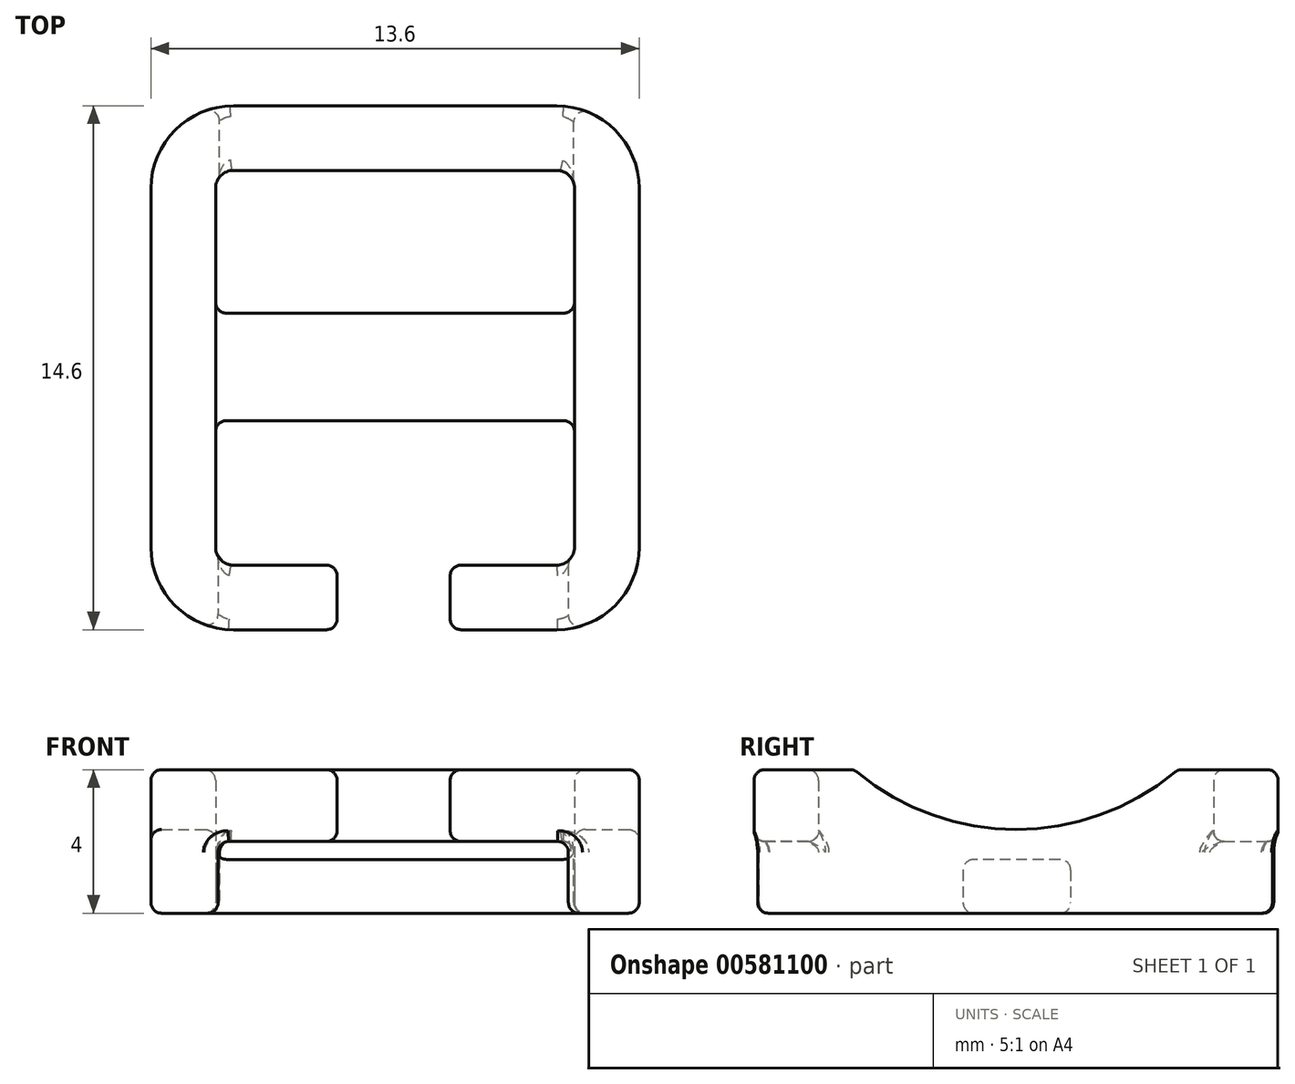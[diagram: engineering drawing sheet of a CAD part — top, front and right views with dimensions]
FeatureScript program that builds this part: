
annotation { "Feature Type Name" : "Feature", "Feature Type Description" : "" }
export const myFeature = defineFeature(function(context is Context, id is Id, definition is map)
    precondition{}
    {
        {
            var Q0;
            Q0=qCreatedBy(makeId("Top.planeOp"),FACE);
            var sketch = newSketch(context, id + "F0", { "sketchPlane" : qUnion([Q0])});
            skPoint(sketch, "E0.middle", {"position": v(0, 0) * mm});
            skLineSegment(sketch, "E1.bottom", {"start": v(-4.5, 5.5) * mm, "end": v(4.5, 5.5) * mm});
            skLineSegment(sketch, "E1.top", {"start": v(-4.5, -5.5) * mm, "end": v(4.5, -5.5) * mm});
            skLineSegment(sketch, "E1.left", {"start": v(-5, 5) * mm, "end": v(-5, -5) * mm});
            skLineSegment(sketch, "E1.right", {"start": v(5, 5) * mm, "end": v(5, -5) * mm});
            skPoint(sketch, "E2.visualSharp", {"position": v(-5, 5.5) * mm});
            skArc(sketch, "E2.filletArc", {"start": v(-4.5, 5.5) * mm, "mid": v(-4.85, 5.35) * mm, "end": v(-5, 5) * mm});
            skPoint(sketch, "E3.visualSharp", {"position": v(5, 5.5) * mm});
            skArc(sketch, "E3.filletArc", {"start": v(5, 5) * mm, "mid": v(4.85, 5.35) * mm, "end": v(4.5, 5.5) * mm});
            skPoint(sketch, "E4.visualSharp", {"position": v(5, -5.5) * mm});
            skArc(sketch, "E4.filletArc", {"start": v(4.5, -5.5) * mm, "mid": v(4.85, -5.35) * mm, "end": v(5, -5) * mm});
            skPoint(sketch, "E5.visualSharp", {"position": v(-5, -5.5) * mm});
            skArc(sketch, "E5.filletArc", {"start": v(-5, -5) * mm, "mid": v(-4.85, -5.35) * mm, "end": v(-4.5, -5.5) * mm});
            skArc(sketch, "E6.0", {"start": v(-4.5, 7.3) * mm, "mid": v(-6.13, 6.63) * mm, "end": v(-6.8, 5) * mm});
            skLineSegment(sketch, "E6.1", {"start": v(-6.8, 5) * mm, "end": v(-6.8, -5) * mm});
            skLineSegment(sketch, "E6.2", {"start": v(-4.5, 7.3) * mm, "end": v(4.5, 7.3) * mm});
            skArc(sketch, "E6.3", {"start": v(-6.8, -5) * mm, "mid": v(-6.13, -6.63) * mm, "end": v(-4.5, -7.3) * mm});
            skArc(sketch, "E6.4", {"start": v(6.8, 5) * mm, "mid": v(6.13, 6.63) * mm, "end": v(4.5, 7.3) * mm});
            skLineSegment(sketch, "E6.5", {"start": v(6.8, 5) * mm, "end": v(6.8, -5) * mm});
            skArc(sketch, "E6.6", {"start": v(4.5, -7.3) * mm, "mid": v(6.13, -6.63) * mm, "end": v(6.8, -5) * mm});
            skLineSegment(sketch, "E6.7", {"start": v(-4.5, -7.3) * mm, "end": v(4.5, -7.3) * mm});
            skSolve(sketch);
        }
        {
            var Q0;
            Q0=makeQuery(id+"F0.imprint","IMPRINT",FACE,{"disambiguationData":[TD([[makeQuery(id+"F0.imprint","IMPRINT",EDGE,{"derivedFrom":sQuery(id+"F0.wireOp",EDGE,"E1.bottom")}),1.0]])]});
            extrude(context, id + "F1", {"entities" : qUnion([Q0]), "endBound" : BoundingType.SYMMETRIC, "depth" : 4 * mm, "offsetDistance" : 25 * mm});
        }
        {
            var Q0;
            Q0=makeQuery(id+"F1.opExtrude","SWEPT_FACE",FACE,{"disambiguationData":[OSD([sQuery(id+"F0.wireOp",EDGE,"E6.5")])]});
            var sketch = newSketch(context, id + "F2", { "sketchPlane" : qUnion([Q0])});
            skCircle(sketch, "E7", {"center": v(0, 7.27) * mm, "radius": 6.94 * mm});
            skSolve(sketch);
        }
        {
            var Q0;
            Q0 = qSketchRegion(id + "F2", true);
            extrude(context, id + "F3", {"entities" : qUnion([Q0]), "operationType" : NewBodyOperationType.REMOVE, "oppositeDirection" : true, "depth" : 17 * mm, "offsetDistance" : 25 * mm});
        }
        {
            var Q0;
            Q0=makeQuery(id+"F1.opExtrude","SWEPT_FACE",FACE,{"disambiguationData":[OSD([sQuery(id+"F0.wireOp",EDGE,"E1.right")])]});
            var sketch = newSketch(context, id + "F4", { "sketchPlane" : qUnion([Q0])});
            skLineSegment(sketch, "E8.bottom", {"start": v(-1.52, -0.5) * mm, "end": v(1.48, -0.5) * mm});
            skLineSegment(sketch, "E8.top", {"start": v(-1.52, -2) * mm, "end": v(1.48, -2) * mm});
            skLineSegment(sketch, "E8.left", {"start": v(-1.52, -0.5) * mm, "end": v(-1.52, -2) * mm});
            skLineSegment(sketch, "E8.right", {"start": v(1.48, -0.5) * mm, "end": v(1.48, -2) * mm});
            skSolve(sketch);
        }
        {
            var Q0;
            Q0=makeQuery(id+"F4.imprint","IMPRINT",FACE,{"disambiguationData":[TD([[makeQuery(id+"F4.imprint","IMPRINT",EDGE,{"derivedFrom":sQuery(id+"F4.wireOp",EDGE,"E8.bottom")}),-1.0]])]});
            var Q1;
            Q1=sQuery(id+"F4.wireOp",EDGE,"E8.bottom");
            var Q2;
            Q2=sQuery(id+"F4.wireOp",EDGE,"E8.right");
            var Q3;
            Q3=sQuery(id+"F4.wireOp",EDGE,"E8.top");
            var Q4;
            Q4=sQuery(id+"F4.wireOp",EDGE,"E8.left");
            extrude(context, id + "F5", {"entities" : qUnion([Q0]), "operationType" : NewBodyOperationType.ADD, "surfaceEntities" : qUnion([Q1, Q2, Q3, Q4]), "depth" : 10.1 * mm, "offsetDistance" : 25 * mm});
        }
        {
            var Q0;
            Q0=makeQuery(id+"F1.opExtrude","SWEPT_FACE",FACE,{"disambiguationData":[OSD([sQuery(id+"F0.wireOp",EDGE,"E6.7")])]});
            var sketch = newSketch(context, id + "F6", { "sketchPlane" : qUnion([Q0])});
            skLineSegment(sketch, "E9.bottom", {"start": v(-4.93, 0) * mm, "end": v(4.83, 0) * mm});
            skLineSegment(sketch, "E9.top", {"start": v(-4.93, -2) * mm, "end": v(4.83, -2) * mm});
            skLineSegment(sketch, "E9.left", {"start": v(-4.93, 0) * mm, "end": v(-4.93, -2) * mm});
            skLineSegment(sketch, "E9.right", {"start": v(4.83, 0) * mm, "end": v(4.83, -2) * mm});
            skSolve(sketch);
        }
        {
            var Q0;
            Q0 = qSketchRegion(id + "F6", true);
            extrude(context, id + "F7", {"entities" : qUnion([Q0]), "operationType" : NewBodyOperationType.REMOVE, "oppositeDirection" : true, "depth" : 2.8 * mm, "offsetDistance" : 25 * mm});
        }
        {
            var Q0;
            Q0=makeQuery(id+"F1.opExtrude","SWEPT_FACE",FACE,{"disambiguationData":[OSD([sQuery(id+"F0.wireOp",EDGE,"E6.2")])]});
            var sketch = newSketch(context, id + "F8", { "sketchPlane" : qUnion([Q0])});
            skLineSegment(sketch, "E10.bottom", {"start": v(-4.98, 0) * mm, "end": v(4.89, 0) * mm});
            skLineSegment(sketch, "E10.top", {"start": v(-4.98, -2) * mm, "end": v(4.89, -2) * mm});
            skLineSegment(sketch, "E10.left", {"start": v(-4.98, 0) * mm, "end": v(-4.98, -2) * mm});
            skLineSegment(sketch, "E10.right", {"start": v(4.89, 0) * mm, "end": v(4.89, -2) * mm});
            skSolve(sketch);
        }
        {
            var Q0;
            Q0 = qSketchRegion(id + "F8", true);
            extrude(context, id + "F9", {"entities" : qUnion([Q0]), "operationType" : NewBodyOperationType.REMOVE, "oppositeDirection" : true, "depth" : 2.4 * mm, "offsetDistance" : 25 * mm});
        }
        {
            var Q0;
            {var subQ0=sQuery(id+"F0.wireOp",EDGE,"E6.7");var subQ1=sQuery(id+"F0.wireOp",EDGE,"E6.3");var subQ2=sQuery(id+"F0.wireOp",EDGE,"E6.1");var subQ3=sQuery(id+"F0.wireOp",EDGE,"E5.filletArc");var subQ4=sQuery(id+"F0.wireOp",EDGE,"E1.top");var subQ5=sQuery(id+"F0.wireOp",EDGE,"E4.filletArc");var subQ6=sQuery(id+"F0.wireOp",EDGE,"E6.5");var subQ7=sQuery(id+"F0.wireOp",EDGE,"E1.left");var subQ8=sQuery(id+"F0.wireOp",EDGE,"E6.6");var subQ9=sQuery(id+"F0.wireOp",EDGE,"E1.right");Q0=makeQuery(id+"F3.boolean.opBoolean","SPLIT",FACE,{"disambiguationData":[TD([makeQuery(id+"F1.opExtrude","SWEPT_FACE",FACE,{"disambiguationData":[OSD([subQ4])]})])],"derivedFrom":makeQuery(id+"F1.opExtrude","CAP_FACE",FACE,{"disambiguationData":[OSD([sQuery(id+"F0.wireOp",EDGE,"E1.bottom"),subQ4,subQ7,subQ9,sQuery(id+"F0.wireOp",EDGE,"E2.filletArc"),sQuery(id+"F0.wireOp",EDGE,"E3.filletArc"),subQ5,subQ3,sQuery(id+"F0.wireOp",EDGE,"E6.0"),subQ2,sQuery(id+"F0.wireOp",EDGE,"E6.2"),subQ1,sQuery(id+"F0.wireOp",EDGE,"E6.4"),subQ6,subQ8,subQ0])],"isStart":false})});}
            var sketch = newSketch(context, id + "F10", { "sketchPlane" : qUnion([Q0])});
            skLineSegment(sketch, "E11.bottom", {"start": v(-1.61, -5.5) * mm, "end": v(1.54, -5.5) * mm});
            skLineSegment(sketch, "E11.top", {"start": v(-1.61, -7.3) * mm, "end": v(1.54, -7.3) * mm});
            skLineSegment(sketch, "E11.left", {"start": v(-1.61, -5.5) * mm, "end": v(-1.61, -7.3) * mm});
            skLineSegment(sketch, "E11.right", {"start": v(1.54, -5.5) * mm, "end": v(1.54, -7.3) * mm});
            skSolve(sketch);
        }
        {
            var Q0;
            Q0 = qSketchRegion(id + "F10", true);
            extrude(context, id + "F11", {"entities" : qUnion([Q0]), "operationType" : NewBodyOperationType.REMOVE, "oppositeDirection" : true, "depth" : 2.3 * mm, "offsetDistance" : 25 * mm});
        }
        {
            var Q0;
            Q0=makeQuery(id+"F5.opExtrude","SWEPT_FACE",FACE,{"disambiguationData":[OSD([sQuery(id+"F4.wireOp",EDGE,"E8.top")])]});
            var Q1;
            Q1=makeQuery(id+"F5.opExtrude","SWEPT_EDGE",EDGE,{"disambiguationData":[OSD([sQuery(id+"F4.wireOp",VERTEX,"E8.right.start")])]});
            var Q2;
            Q2=makeQuery(id+"F5.opExtrude","SWEPT_FACE",FACE,{"disambiguationData":[OSD([sQuery(id+"F4.wireOp",EDGE,"E8.right")])]});
            var Q3;
            Q3=makeQuery(id+"F5.opExtrude","SWEPT_EDGE",EDGE,{"disambiguationData":[OSD([sQuery(id+"F4.wireOp",VERTEX,"E8.top.end")])]});
            var Q4;
            Q4=makeQuery(id+"F5.opExtrude","SWEPT_FACE",FACE,{"disambiguationData":[OSD([sQuery(id+"F4.wireOp",EDGE,"E8.bottom")])]});
            var Q5;
            Q5=makeQuery(id+"F5.opExtrude","SWEPT_EDGE",EDGE,{"disambiguationData":[OSD([sQuery(id+"F4.wireOp",VERTEX,"E8.left.start")])]});
            var Q6;
            Q6=makeQuery(id+"F1.opExtrude","CAP_EDGE",EDGE,{"disambiguationData":[OSD([sQuery(id+"F0.wireOp",EDGE,"E6.2")])],"isStart":false});
            var Q7;
            Q7=makeQuery(id+"F3.boolean.opBoolean","INTERSECT",EDGE,{"derivedFrom":[makeQuery(id+"F1.opExtrude","SWEPT_FACE",FACE,{"disambiguationData":[OSD([sQuery(id+"F0.wireOp",EDGE,"E1.left")])]}),makeQuery(id+"F3.opExtrude","SWEPT_FACE",FACE,{"disambiguationData":[OSD([sQuery(id+"F2.wireOp",EDGE,"E7")])]})]});
            var Q8;
            Q8=makeQuery(id+"F1.opExtrude","SWEPT_FACE",FACE,{"disambiguationData":[OSD([sQuery(id+"F0.wireOp",EDGE,"E1.left")])]});
            var Q9;
            Q9=makeQuery(id+"F1.opExtrude","CAP_EDGE",EDGE,{"disambiguationData":[OSD([sQuery(id+"F0.wireOp",EDGE,"E1.left")])],"isStart":true});
            var Q10;
            Q10=makeQuery(id+"F1.opExtrude","CAP_EDGE",EDGE,{"disambiguationData":[OSD([sQuery(id+"F0.wireOp",EDGE,"E1.bottom")])],"isStart":false});
            var Q11;
            Q11=makeQuery(id+"F1.opExtrude","SWEPT_FACE",FACE,{"disambiguationData":[OSD([sQuery(id+"F0.wireOp",EDGE,"E1.bottom")])]});
            var Q12;
            Q12=makeQuery(id+"F3.boolean.opBoolean","COPY",EDGE,{"derivedFrom":makeQuery(id+"F3.opExtrude","CAP_EDGE",EDGE,{"disambiguationData":[OSD([sQuery(id+"F2.wireOp",EDGE,"E7")])],"isStart":true})});
            var Q13;
            Q13=makeQuery(id+"F1.opExtrude","CAP_EDGE",EDGE,{"disambiguationData":[OSD([sQuery(id+"F0.wireOp",EDGE,"E6.5")])],"isStart":true});
            var Q14;
            Q14=makeQuery(id+"F7.boolean.opBoolean","COPY",FACE,{"derivedFrom":makeQuery(id+"F7.opExtrude","SWEPT_FACE",FACE,{"disambiguationData":[OSD([sQuery(id+"F6.wireOp",EDGE,"E9.right")])]})});
            var Q15;
            Q15=makeQuery(id+"F9.boolean.opBoolean","COPY",FACE,{"derivedFrom":makeQuery(id+"F9.opExtrude","SWEPT_FACE",FACE,{"disambiguationData":[OSD([sQuery(id+"F8.wireOp",EDGE,"E10.right")])]})});
            var Q16;
            {var subQ0=sQuery(id+"F6.wireOp",EDGE,"E9.bottom");Q16=makeQuery(id+"F11.boolean.opBoolean","SPLIT",EDGE,{"disambiguationData":[TD([makeQuery(id+"F1.opExtrude","SWEPT_FACE",FACE,{"disambiguationData":[OSD([sQuery(id+"F0.wireOp",EDGE,"E6.6")])]})])],"derivedFrom":makeQuery(id+"F7.boolean.opBoolean","COPY",EDGE,{"derivedFrom":makeQuery(id+"F7.opExtrude","CAP_EDGE",EDGE,{"disambiguationData":[OSD([subQ0])],"isStart":true})})});}
            var Q17;
            Q17=makeQuery(id+"F3.boolean.opBoolean","INTERSECT",EDGE,{"disambiguationData":[OD(2.0)],"derivedFrom":[makeQuery(id+"F1.opExtrude","CAP_FACE",FACE,{"disambiguationData":[OSD([sQuery(id+"F0.wireOp",EDGE,"E1.bottom"),sQuery(id+"F0.wireOp",EDGE,"E1.top"),sQuery(id+"F0.wireOp",EDGE,"E1.left"),sQuery(id+"F0.wireOp",EDGE,"E1.right"),sQuery(id+"F0.wireOp",EDGE,"E2.filletArc"),sQuery(id+"F0.wireOp",EDGE,"E3.filletArc"),sQuery(id+"F0.wireOp",EDGE,"E4.filletArc"),sQuery(id+"F0.wireOp",EDGE,"E5.filletArc"),sQuery(id+"F0.wireOp",EDGE,"E6.0"),sQuery(id+"F0.wireOp",EDGE,"E6.1"),sQuery(id+"F0.wireOp",EDGE,"E6.2"),sQuery(id+"F0.wireOp",EDGE,"E6.3"),sQuery(id+"F0.wireOp",EDGE,"E6.4"),sQuery(id+"F0.wireOp",EDGE,"E6.5"),sQuery(id+"F0.wireOp",EDGE,"E6.6"),sQuery(id+"F0.wireOp",EDGE,"E6.7")])],"isStart":false}),makeQuery(id+"F3.opExtrude","SWEPT_FACE",FACE,{"disambiguationData":[OSD([sQuery(id+"F2.wireOp",EDGE,"E7")])]})]});
            var Q18;
            Q18=makeQuery(id+"F11.boolean.opBoolean","COPY",FACE,{"derivedFrom":makeQuery(id+"F11.opExtrude","SWEPT_FACE",FACE,{"disambiguationData":[OSD([sQuery(id+"F10.wireOp",EDGE,"E11.left")])]})});
            var Q19;
            Q19=makeQuery(id+"F1.opExtrude","SWEPT_FACE",FACE,{"disambiguationData":[OSD([sQuery(id+"F0.wireOp",EDGE,"E1.right")])]});
            var Q20;
            Q20=makeQuery(id+"F7.boolean.opBoolean","COPY",EDGE,{"derivedFrom":makeQuery(id+"F7.opExtrude","SWEPT_EDGE",EDGE,{"disambiguationData":[OSD([sQuery(id+"F6.wireOp",EDGE,"E9.top"),sQuery(id+"F6.wireOp",EDGE,"E9.left")])]})});
            var Q21;
            Q21=makeQuery(id+"F9.boolean.opBoolean","INTERSECT",EDGE,{"derivedFrom":[makeQuery(id+"F1.opExtrude","SWEPT_FACE",FACE,{"disambiguationData":[OSD([sQuery(id+"F0.wireOp",EDGE,"E1.bottom")])]}),makeQuery(id+"F9.opExtrude","SWEPT_FACE",FACE,{"disambiguationData":[OSD([sQuery(id+"F8.wireOp",EDGE,"E10.bottom")])]})]});
            var Q22;
            Q22=makeQuery(id+"F9.boolean.opBoolean","COPY",EDGE,{"derivedFrom":makeQuery(id+"F9.opExtrude","SWEPT_EDGE",EDGE,{"disambiguationData":[OSD([sQuery(id+"F8.wireOp",EDGE,"E10.top"),sQuery(id+"F8.wireOp",EDGE,"E10.right")])]})});
            var Q23;
            Q23=makeQuery(id+"F7.boolean.opBoolean","COPY",FACE,{"derivedFrom":makeQuery(id+"F7.opExtrude","SWEPT_FACE",FACE,{"disambiguationData":[OSD([sQuery(id+"F6.wireOp",EDGE,"E9.left")])]})});
            var Q24;
            Q24=makeQuery(id+"F1.opExtrude","SWEPT_FACE",FACE,{"disambiguationData":[OSD([sQuery(id+"F0.wireOp",EDGE,"E2.filletArc")])]});
            var Q25;
            Q25=makeQuery(id+"F3.boolean.opBoolean","INTERSECT",EDGE,{"derivedFrom":[makeQuery(id+"F1.opExtrude","SWEPT_FACE",FACE,{"disambiguationData":[OSD([sQuery(id+"F0.wireOp",EDGE,"E1.right")])]}),makeQuery(id+"F3.opExtrude","SWEPT_FACE",FACE,{"disambiguationData":[OSD([sQuery(id+"F2.wireOp",EDGE,"E7")])]})]});
            var Q26;
            Q26=makeQuery(id+"F1.opExtrude","SWEPT_FACE",FACE,{"disambiguationData":[OSD([sQuery(id+"F0.wireOp",EDGE,"E6.1")])]});
            var Q27;
            Q27=makeQuery(id+"F3.boolean.opBoolean","INTERSECT",EDGE,{"derivedFrom":[makeQuery(id+"F1.opExtrude","SWEPT_FACE",FACE,{"disambiguationData":[OSD([sQuery(id+"F0.wireOp",EDGE,"E6.1")])]}),makeQuery(id+"F3.opExtrude","SWEPT_FACE",FACE,{"disambiguationData":[OSD([sQuery(id+"F2.wireOp",EDGE,"E7")])]})]});
            var Q28;
            Q28=makeQuery(id+"F1.opExtrude","SWEPT_FACE",FACE,{"disambiguationData":[OSD([sQuery(id+"F0.wireOp",EDGE,"E6.5")])]});
            var Q29;
            {var subQ0=sQuery(id+"F0.wireOp",EDGE,"E6.4");var subQ1=sQuery(id+"F0.wireOp",EDGE,"E6.2");var subQ2=sQuery(id+"F0.wireOp",EDGE,"E6.0");var subQ3=sQuery(id+"F0.wireOp",EDGE,"E3.filletArc");var subQ4=sQuery(id+"F0.wireOp",EDGE,"E6.1");var subQ5=sQuery(id+"F0.wireOp",EDGE,"E1.bottom");var subQ6=sQuery(id+"F0.wireOp",EDGE,"E1.right");var subQ7=sQuery(id+"F0.wireOp",EDGE,"E6.5");var subQ8=sQuery(id+"F0.wireOp",EDGE,"E1.left");var subQ9=sQuery(id+"F0.wireOp",EDGE,"E2.filletArc");Q29=makeQuery(id+"F3.boolean.opBoolean","SPLIT",FACE,{"disambiguationData":[TD([makeQuery(id+"F1.opExtrude","SWEPT_FACE",FACE,{"disambiguationData":[OSD([subQ5])]})])],"derivedFrom":makeQuery(id+"F1.opExtrude","CAP_FACE",FACE,{"disambiguationData":[OSD([subQ5,sQuery(id+"F0.wireOp",EDGE,"E1.top"),subQ8,subQ6,subQ9,subQ3,sQuery(id+"F0.wireOp",EDGE,"E4.filletArc"),sQuery(id+"F0.wireOp",EDGE,"E5.filletArc"),subQ2,subQ4,subQ1,sQuery(id+"F0.wireOp",EDGE,"E6.3"),subQ0,subQ7,sQuery(id+"F0.wireOp",EDGE,"E6.6"),sQuery(id+"F0.wireOp",EDGE,"E6.7")])],"isStart":false})});}
            var Q30;
            {var subQ1=sQuery(id+"F0.wireOp",EDGE,"E1.right");Q30=makeQuery(id+"F3.boolean.opBoolean","COPY",FACE,{"disambiguationData":[TD([makeQuery(id+"F1.opExtrude","SWEPT_FACE",FACE,{"disambiguationData":[OSD([subQ1])]})])],"derivedFrom":makeQuery(id+"F3.opExtrude","SWEPT_FACE",FACE,{"disambiguationData":[OSD([sQuery(id+"F2.wireOp",EDGE,"E7")])]})});}
            var Q31;
            {var subQ1=sQuery(id+"F0.wireOp",EDGE,"E1.left");Q31=makeQuery(id+"F3.boolean.opBoolean","COPY",FACE,{"disambiguationData":[TD([makeQuery(id+"F1.opExtrude","SWEPT_FACE",FACE,{"disambiguationData":[OSD([subQ1])]})])],"derivedFrom":makeQuery(id+"F3.opExtrude","SWEPT_FACE",FACE,{"disambiguationData":[OSD([sQuery(id+"F2.wireOp",EDGE,"E7")])]})});}
            var Q32;
            Q32=makeQuery(id+"F1.opExtrude","SWEPT_FACE",FACE,{"disambiguationData":[OSD([sQuery(id+"F0.wireOp",EDGE,"E6.3")])]});
            var Q33;
            Q33=makeQuery(id+"F1.opExtrude","SWEPT_FACE",FACE,{"disambiguationData":[OSD([sQuery(id+"F0.wireOp",EDGE,"E6.6")])]});
            var Q34;
            Q34=makeQuery(id+"F1.opExtrude","CAP_EDGE",EDGE,{"disambiguationData":[OSD([sQuery(id+"F0.wireOp",EDGE,"E6.6")])],"isStart":true});
            var Q35;
            Q35=makeQuery(id+"F1.opExtrude","SWEPT_FACE",FACE,{"disambiguationData":[OSD([sQuery(id+"F0.wireOp",EDGE,"E6.0")])]});
            var Q36;
            Q36=makeQuery(id+"F1.opExtrude","SWEPT_FACE",FACE,{"disambiguationData":[OSD([sQuery(id+"F0.wireOp",EDGE,"E6.2")])]});
            var Q37;
            Q37=makeQuery(id+"F1.opExtrude","SWEPT_FACE",FACE,{"disambiguationData":[OSD([sQuery(id+"F0.wireOp",EDGE,"E6.4")])]});
            var Q38;
            {var subQ0=sQuery(id+"F0.wireOp",EDGE,"E6.0");var subQ1=sQuery(id+"F0.wireOp",EDGE,"E2.filletArc");var subQ2=sQuery(id+"F0.wireOp",EDGE,"E5.filletArc");var subQ3=sQuery(id+"F0.wireOp",EDGE,"E1.left");var subQ4=sQuery(id+"F0.wireOp",EDGE,"E6.1");var subQ5=sQuery(id+"F0.wireOp",EDGE,"E6.3");Q38=makeQuery(id+"F9.boolean.opBoolean","SPLIT",FACE,{"disambiguationData":[TD([makeQuery(id+"F1.opExtrude","SWEPT_FACE",FACE,{"disambiguationData":[OSD([subQ3])]})])],"derivedFrom":makeQuery(id+"F1.opExtrude","CAP_FACE",FACE,{"disambiguationData":[OSD([sQuery(id+"F0.wireOp",EDGE,"E1.bottom"),sQuery(id+"F0.wireOp",EDGE,"E1.top"),subQ3,sQuery(id+"F0.wireOp",EDGE,"E1.right"),subQ1,sQuery(id+"F0.wireOp",EDGE,"E3.filletArc"),sQuery(id+"F0.wireOp",EDGE,"E4.filletArc"),subQ2,subQ0,subQ4,sQuery(id+"F0.wireOp",EDGE,"E6.2"),subQ5,sQuery(id+"F0.wireOp",EDGE,"E6.4"),sQuery(id+"F0.wireOp",EDGE,"E6.5"),sQuery(id+"F0.wireOp",EDGE,"E6.6"),sQuery(id+"F0.wireOp",EDGE,"E6.7")])],"isStart":true})});}
            var Q39;
            {var subQ0=sQuery(id+"F0.wireOp",EDGE,"E6.4");var subQ1=sQuery(id+"F0.wireOp",EDGE,"E4.filletArc");var subQ2=sQuery(id+"F0.wireOp",EDGE,"E3.filletArc");var subQ3=sQuery(id+"F0.wireOp",EDGE,"E1.right");var subQ4=sQuery(id+"F0.wireOp",EDGE,"E6.6");var subQ5=sQuery(id+"F0.wireOp",EDGE,"E6.5");Q39=makeQuery(id+"F9.boolean.opBoolean","SPLIT",FACE,{"disambiguationData":[TD([makeQuery(id+"F1.opExtrude","SWEPT_FACE",FACE,{"disambiguationData":[OSD([subQ3])]})])],"derivedFrom":makeQuery(id+"F1.opExtrude","CAP_FACE",FACE,{"disambiguationData":[OSD([sQuery(id+"F0.wireOp",EDGE,"E1.bottom"),sQuery(id+"F0.wireOp",EDGE,"E1.top"),sQuery(id+"F0.wireOp",EDGE,"E1.left"),subQ3,sQuery(id+"F0.wireOp",EDGE,"E2.filletArc"),subQ2,subQ1,sQuery(id+"F0.wireOp",EDGE,"E5.filletArc"),sQuery(id+"F0.wireOp",EDGE,"E6.0"),sQuery(id+"F0.wireOp",EDGE,"E6.1"),sQuery(id+"F0.wireOp",EDGE,"E6.2"),sQuery(id+"F0.wireOp",EDGE,"E6.3"),subQ0,subQ5,subQ4,sQuery(id+"F0.wireOp",EDGE,"E6.7")])],"isStart":true})});}
            var Q40;
            Q40=makeQuery(id+"F11.boolean.opBoolean","COPY",FACE,{"derivedFrom":makeQuery(id+"F11.opExtrude","SWEPT_FACE",FACE,{"disambiguationData":[OSD([sQuery(id+"F10.wireOp",EDGE,"E11.right")])]})});
            var Q41;
            Q41=makeQuery(id+"F11.boolean.opBoolean","COPY",EDGE,{"derivedFrom":makeQuery(id+"F11.opExtrude","SWEPT_EDGE",EDGE,{"disambiguationData":[OSD([sQuery(id+"F0.wireOp",EDGE,"E6.7"),sQuery(id+"F10.wireOp",EDGE,"E11.top"),sQuery(id+"F10.wireOp",EDGE,"E11.left")])]})});
            var Q42;
            {var subQ0=sQuery(id+"F0.wireOp",EDGE,"E6.5");var subQ2=sQuery(id+"F0.wireOp",EDGE,"E1.right");var subQ3=makeQuery(id+"F1.opExtrude","SWEPT_FACE",FACE,{"disambiguationData":[OSD([subQ2])]});var subQ4=sQuery(id+"F0.wireOp",EDGE,"E6.6");var subQ6=sQuery(id+"F0.wireOp",EDGE,"E4.filletArc");var subQ8=sQuery(id+"F0.wireOp",EDGE,"E1.top");var subQ9=makeQuery(id+"F1.opExtrude","SWEPT_FACE",FACE,{"disambiguationData":[OSD([subQ8])]});var subQ10=sQuery(id+"F0.wireOp",EDGE,"E6.7");var subQ12=sQuery(id+"F0.wireOp",EDGE,"E6.3");var subQ13=sQuery(id+"F0.wireOp",EDGE,"E6.1");var subQ14=sQuery(id+"F0.wireOp",EDGE,"E5.filletArc");var subQ15=sQuery(id+"F0.wireOp",EDGE,"E1.left");var subQ16=makeQuery(id+"F1.opExtrude","CAP_FACE",FACE,{"disambiguationData":[OSD([sQuery(id+"F0.wireOp",EDGE,"E1.bottom"),subQ8,subQ15,subQ2,sQuery(id+"F0.wireOp",EDGE,"E2.filletArc"),sQuery(id+"F0.wireOp",EDGE,"E3.filletArc"),subQ6,subQ14,sQuery(id+"F0.wireOp",EDGE,"E6.0"),subQ13,sQuery(id+"F0.wireOp",EDGE,"E6.2"),subQ12,sQuery(id+"F0.wireOp",EDGE,"E6.4"),subQ0,subQ4,subQ10])],"isStart":false});Q42=makeQuery(id+"F11.boolean.opBoolean","SPLIT",FACE,{"disambiguationData":[TD([subQ3])],"derivedFrom":makeQuery(id+"F3.boolean.opBoolean","SPLIT",FACE,{"disambiguationData":[TD([subQ9])],"derivedFrom":subQ16})});}
            var Q43;
            {var subQ0=sQuery(id+"F0.wireOp",EDGE,"E6.1");var subQ2=sQuery(id+"F0.wireOp",EDGE,"E5.filletArc");var subQ4=sQuery(id+"F0.wireOp",EDGE,"E1.left");var subQ5=makeQuery(id+"F1.opExtrude","SWEPT_FACE",FACE,{"disambiguationData":[OSD([subQ4])]});var subQ6=sQuery(id+"F0.wireOp",EDGE,"E1.top");var subQ7=makeQuery(id+"F1.opExtrude","SWEPT_FACE",FACE,{"disambiguationData":[OSD([subQ6])]});var subQ8=sQuery(id+"F0.wireOp",EDGE,"E6.3");var subQ10=sQuery(id+"F0.wireOp",EDGE,"E6.7");var subQ12=sQuery(id+"F0.wireOp",EDGE,"E6.6");var subQ13=sQuery(id+"F0.wireOp",EDGE,"E6.5");var subQ14=sQuery(id+"F0.wireOp",EDGE,"E4.filletArc");var subQ15=sQuery(id+"F0.wireOp",EDGE,"E1.right");var subQ16=makeQuery(id+"F1.opExtrude","CAP_FACE",FACE,{"disambiguationData":[OSD([sQuery(id+"F0.wireOp",EDGE,"E1.bottom"),subQ6,subQ4,subQ15,sQuery(id+"F0.wireOp",EDGE,"E2.filletArc"),sQuery(id+"F0.wireOp",EDGE,"E3.filletArc"),subQ14,subQ2,sQuery(id+"F0.wireOp",EDGE,"E6.0"),subQ0,sQuery(id+"F0.wireOp",EDGE,"E6.2"),subQ8,sQuery(id+"F0.wireOp",EDGE,"E6.4"),subQ13,subQ12,subQ10])],"isStart":false});Q43=makeQuery(id+"F11.boolean.opBoolean","SPLIT",FACE,{"disambiguationData":[TD([subQ5])],"derivedFrom":makeQuery(id+"F3.boolean.opBoolean","SPLIT",FACE,{"disambiguationData":[TD([subQ7])],"derivedFrom":subQ16})});}
            var Q44;
            {var subQ0=sQuery(id+"F0.wireOp",EDGE,"E5.filletArc");var subQ1=sQuery(id+"F0.wireOp",EDGE,"E1.top");Q44=makeQuery(id+"F11.boolean.opBoolean","SPLIT",FACE,{"disambiguationData":[TD([makeQuery(id+"F1.opExtrude","SWEPT_FACE",FACE,{"disambiguationData":[OSD([subQ0])]})])],"derivedFrom":makeQuery(id+"F1.opExtrude","SWEPT_FACE",FACE,{"disambiguationData":[OSD([subQ1])]})});}
            var Q45;
            {var subQ0=sQuery(id+"F0.wireOp",EDGE,"E4.filletArc");var subQ1=sQuery(id+"F0.wireOp",EDGE,"E1.top");Q45=makeQuery(id+"F11.boolean.opBoolean","SPLIT",FACE,{"disambiguationData":[TD([makeQuery(id+"F1.opExtrude","SWEPT_FACE",FACE,{"disambiguationData":[OSD([subQ0])]})])],"derivedFrom":makeQuery(id+"F1.opExtrude","SWEPT_FACE",FACE,{"disambiguationData":[OSD([subQ1])]})});}
            var Q46;
            {var subQ0=sQuery(id+"F0.wireOp",EDGE,"E5.filletArc");var subQ1=sQuery(id+"F0.wireOp",EDGE,"E1.top");Q46=makeQuery(id+"F11.boolean.opBoolean","SPLIT",EDGE,{"disambiguationData":[TD([makeQuery(id+"F1.opExtrude","SWEPT_FACE",FACE,{"disambiguationData":[OSD([subQ0])]})])],"derivedFrom":makeQuery(id+"F1.opExtrude","CAP_EDGE",EDGE,{"disambiguationData":[OSD([subQ1])],"isStart":false})});}
            var Q47;
            {var subQ0=sQuery(id+"F0.wireOp",EDGE,"E6.7");var subQ1=sQuery(id+"F0.wireOp",EDGE,"E6.3");Q47=makeQuery(id+"F11.boolean.opBoolean","SPLIT",FACE,{"disambiguationData":[TD([makeQuery(id+"F1.opExtrude","SWEPT_FACE",FACE,{"disambiguationData":[OSD([subQ1])]})])],"derivedFrom":makeQuery(id+"F1.opExtrude","SWEPT_FACE",FACE,{"disambiguationData":[OSD([subQ0])]})});}
            var Q48;
            {var subQ0=sQuery(id+"F0.wireOp",EDGE,"E6.7");var subQ1=sQuery(id+"F0.wireOp",EDGE,"E6.6");Q48=makeQuery(id+"F11.boolean.opBoolean","SPLIT",FACE,{"disambiguationData":[TD([makeQuery(id+"F1.opExtrude","SWEPT_FACE",FACE,{"disambiguationData":[OSD([subQ1])]})])],"derivedFrom":makeQuery(id+"F1.opExtrude","SWEPT_FACE",FACE,{"disambiguationData":[OSD([subQ0])]})});}
            var Q49;
            {var subQ0=sQuery(id+"F0.wireOp",EDGE,"E6.7");var subQ1=sQuery(id+"F0.wireOp",EDGE,"E6.6");Q49=makeQuery(id+"F11.boolean.opBoolean","SPLIT",EDGE,{"disambiguationData":[TD([makeQuery(id+"F1.opExtrude","SWEPT_FACE",FACE,{"disambiguationData":[OSD([subQ1])]})])],"derivedFrom":makeQuery(id+"F1.opExtrude","CAP_EDGE",EDGE,{"disambiguationData":[OSD([subQ0])],"isStart":false})});}
            var Q50;
            Q50=makeQuery(id+"F5.opExtrude","SWEPT_FACE",FACE,{"disambiguationData":[OSD([sQuery(id+"F4.wireOp",EDGE,"E8.left")])]});
            var Q51;
            Q51=makeQuery(id+"F5.opExtrude","SWEPT_EDGE",EDGE,{"disambiguationData":[OSD([sQuery(id+"F4.wireOp",VERTEX,"E8.left.end")])]});
            var Q52;
            Q52=makeQuery(id+"F9.boolean.opBoolean","COPY",EDGE,{"derivedFrom":makeQuery(id+"F9.opExtrude","SWEPT_EDGE",EDGE,{"disambiguationData":[OSD([sQuery(id+"F8.wireOp",EDGE,"E10.bottom"),sQuery(id+"F8.wireOp",EDGE,"E10.left")])]})});
            var Q53;
            Q53=makeQuery(id+"F1.opExtrude","CAP_EDGE",EDGE,{"disambiguationData":[OSD([sQuery(id+"F0.wireOp",EDGE,"E6.1")])],"isStart":true});
            var Q54;
            Q54=makeQuery(id+"F9.boolean.opBoolean","COPY",EDGE,{"derivedFrom":makeQuery(id+"F9.opExtrude","CAP_EDGE",EDGE,{"disambiguationData":[OSD([sQuery(id+"F8.wireOp",EDGE,"E10.bottom")])],"isStart":true})});
            var Q55;
            Q55=makeQuery(id+"F1.opExtrude","SWEPT_EDGE",EDGE,{"disambiguationData":[OSD([sQuery(id+"F0.wireOp",EDGE,"E6.0"),sQuery(id+"F0.wireOp",EDGE,"E6.1")])]});
            var Q56;
            Q56=makeQuery(id+"F1.opExtrude","CAP_EDGE",EDGE,{"disambiguationData":[OSD([sQuery(id+"F0.wireOp",EDGE,"E6.4")])],"isStart":false});
            var Q57;
            Q57=makeQuery(id+"F9.boolean.opBoolean","COPY",FACE,{"derivedFrom":makeQuery(id+"F9.opExtrude","SWEPT_FACE",FACE,{"disambiguationData":[OSD([sQuery(id+"F8.wireOp",EDGE,"E10.left")])]})});
            var Q58;
            Q58=makeQuery(id+"F1.opExtrude","CAP_EDGE",EDGE,{"disambiguationData":[OSD([sQuery(id+"F0.wireOp",EDGE,"E1.right")])],"isStart":true});
            var Q59;
            Q59=makeQuery(id+"F9.boolean.opBoolean","COPY",EDGE,{"derivedFrom":makeQuery(id+"F9.opExtrude","SWEPT_EDGE",EDGE,{"disambiguationData":[OSD([sQuery(id+"F8.wireOp",EDGE,"E10.bottom"),sQuery(id+"F8.wireOp",EDGE,"E10.right")])]})});
            var Q60;
            Q60=makeQuery(id+"F3.boolean.opBoolean","INTERSECT",EDGE,{"disambiguationData":[OD(3.0)],"derivedFrom":[makeQuery(id+"F1.opExtrude","CAP_FACE",FACE,{"disambiguationData":[OSD([sQuery(id+"F0.wireOp",EDGE,"E1.bottom"),sQuery(id+"F0.wireOp",EDGE,"E1.top"),sQuery(id+"F0.wireOp",EDGE,"E1.left"),sQuery(id+"F0.wireOp",EDGE,"E1.right"),sQuery(id+"F0.wireOp",EDGE,"E2.filletArc"),sQuery(id+"F0.wireOp",EDGE,"E3.filletArc"),sQuery(id+"F0.wireOp",EDGE,"E4.filletArc"),sQuery(id+"F0.wireOp",EDGE,"E5.filletArc"),sQuery(id+"F0.wireOp",EDGE,"E6.0"),sQuery(id+"F0.wireOp",EDGE,"E6.1"),sQuery(id+"F0.wireOp",EDGE,"E6.2"),sQuery(id+"F0.wireOp",EDGE,"E6.3"),sQuery(id+"F0.wireOp",EDGE,"E6.4"),sQuery(id+"F0.wireOp",EDGE,"E6.5"),sQuery(id+"F0.wireOp",EDGE,"E6.6"),sQuery(id+"F0.wireOp",EDGE,"E6.7")])],"isStart":false}),makeQuery(id+"F3.opExtrude","SWEPT_FACE",FACE,{"disambiguationData":[OSD([sQuery(id+"F2.wireOp",EDGE,"E7")])]})]});
            var Q61;
            Q61=makeQuery(id+"F1.opExtrude","SWEPT_EDGE",EDGE,{"disambiguationData":[OSD([sQuery(id+"F0.wireOp",EDGE,"E6.5"),sQuery(id+"F0.wireOp",EDGE,"E6.6")])]});
            var Q62;
            Q62=makeQuery(id+"F1.opExtrude","CAP_EDGE",EDGE,{"disambiguationData":[OSD([sQuery(id+"F0.wireOp",EDGE,"E6.3")])],"isStart":false});
            var Q63;
            Q63=makeQuery(id+"F1.opExtrude","CAP_EDGE",EDGE,{"disambiguationData":[OSD([sQuery(id+"F0.wireOp",EDGE,"E2.filletArc")])],"isStart":false});
            var Q64;
            Q64=makeQuery(id+"F3.boolean.opBoolean","INTERSECT",EDGE,{"disambiguationData":[OD(1.0)],"derivedFrom":[makeQuery(id+"F1.opExtrude","CAP_FACE",FACE,{"disambiguationData":[OSD([sQuery(id+"F0.wireOp",EDGE,"E1.bottom"),sQuery(id+"F0.wireOp",EDGE,"E1.top"),sQuery(id+"F0.wireOp",EDGE,"E1.left"),sQuery(id+"F0.wireOp",EDGE,"E1.right"),sQuery(id+"F0.wireOp",EDGE,"E2.filletArc"),sQuery(id+"F0.wireOp",EDGE,"E3.filletArc"),sQuery(id+"F0.wireOp",EDGE,"E4.filletArc"),sQuery(id+"F0.wireOp",EDGE,"E5.filletArc"),sQuery(id+"F0.wireOp",EDGE,"E6.0"),sQuery(id+"F0.wireOp",EDGE,"E6.1"),sQuery(id+"F0.wireOp",EDGE,"E6.2"),sQuery(id+"F0.wireOp",EDGE,"E6.3"),sQuery(id+"F0.wireOp",EDGE,"E6.4"),sQuery(id+"F0.wireOp",EDGE,"E6.5"),sQuery(id+"F0.wireOp",EDGE,"E6.6"),sQuery(id+"F0.wireOp",EDGE,"E6.7")])],"isStart":false}),makeQuery(id+"F3.opExtrude","SWEPT_FACE",FACE,{"disambiguationData":[OSD([sQuery(id+"F2.wireOp",EDGE,"E7")])]})]});
            var Q65;
            Q65=makeQuery(id+"F1.opExtrude","SWEPT_FACE",FACE,{"disambiguationData":[OSD([sQuery(id+"F0.wireOp",EDGE,"E3.filletArc")])]});
            var Q66;
            Q66=makeQuery(id+"F1.opExtrude","SWEPT_EDGE",EDGE,{"disambiguationData":[OSD([sQuery(id+"F0.wireOp",EDGE,"E1.bottom"),sQuery(id+"F0.wireOp",EDGE,"E2.filletArc")])]});
            var Q67;
            Q67=makeQuery(id+"F11.boolean.opBoolean","COPY",EDGE,{"derivedFrom":makeQuery(id+"F11.opExtrude","SWEPT_EDGE",EDGE,{"disambiguationData":[OSD([sQuery(id+"F0.wireOp",EDGE,"E1.top"),sQuery(id+"F10.wireOp",EDGE,"E11.bottom"),sQuery(id+"F10.wireOp",EDGE,"E11.left")])]})});
            var Q68;
            Q68=makeQuery(id+"F1.opExtrude","SWEPT_EDGE",EDGE,{"disambiguationData":[OSD([sQuery(id+"F0.wireOp",EDGE,"E6.4"),sQuery(id+"F0.wireOp",EDGE,"E6.5")])]});
            var Q69;
            Q69=makeQuery(id+"F7.boolean.opBoolean","COPY",EDGE,{"derivedFrom":makeQuery(id+"F7.opExtrude","SWEPT_EDGE",EDGE,{"disambiguationData":[OSD([sQuery(id+"F6.wireOp",EDGE,"E9.top"),sQuery(id+"F6.wireOp",EDGE,"E9.right")])]})});
            var Q70;
            Q70=makeQuery(id+"F1.opExtrude","CAP_EDGE",EDGE,{"disambiguationData":[OSD([sQuery(id+"F0.wireOp",EDGE,"E6.6")])],"isStart":false});
            var Q71;
            Q71=makeQuery(id+"F1.opExtrude","SWEPT_FACE",FACE,{"disambiguationData":[OSD([sQuery(id+"F0.wireOp",EDGE,"E4.filletArc")])]});
            var Q72;
            Q72=makeQuery(id+"F7.boolean.opBoolean","COPY",EDGE,{"derivedFrom":makeQuery(id+"F7.opExtrude","SWEPT_EDGE",EDGE,{"disambiguationData":[OSD([sQuery(id+"F6.wireOp",EDGE,"E9.bottom"),sQuery(id+"F6.wireOp",EDGE,"E9.left")])]})});
            var Q73;
            Q73=makeQuery(id+"F9.boolean.opBoolean","COPY",EDGE,{"derivedFrom":makeQuery(id+"F9.opExtrude","SWEPT_EDGE",EDGE,{"disambiguationData":[OSD([sQuery(id+"F8.wireOp",EDGE,"E10.top"),sQuery(id+"F8.wireOp",EDGE,"E10.left")])]})});
            var Q74;
            Q74=makeQuery(id+"F11.boolean.opBoolean","COPY",EDGE,{"derivedFrom":makeQuery(id+"F11.opExtrude","SWEPT_EDGE",EDGE,{"disambiguationData":[OSD([sQuery(id+"F0.wireOp",EDGE,"E1.top"),sQuery(id+"F10.wireOp",EDGE,"E11.bottom"),sQuery(id+"F10.wireOp",EDGE,"E11.right")])]})});
            var Q75;
            Q75=makeQuery(id+"F1.opExtrude","SWEPT_EDGE",EDGE,{"disambiguationData":[OSD([sQuery(id+"F0.wireOp",EDGE,"E6.1"),sQuery(id+"F0.wireOp",EDGE,"E6.3")])]});
            var Q76;
            Q76=makeQuery(id+"F9.boolean.opBoolean","COPY",FACE,{"derivedFrom":makeQuery(id+"F9.opExtrude","SWEPT_FACE",FACE,{"disambiguationData":[OSD([sQuery(id+"F8.wireOp",EDGE,"E10.bottom")])]})});
            var Q77;
            Q77=makeQuery(id+"F1.opExtrude","SWEPT_EDGE",EDGE,{"disambiguationData":[OSD([sQuery(id+"F0.wireOp",EDGE,"E1.left"),sQuery(id+"F0.wireOp",EDGE,"E2.filletArc")])]});
            var Q78;
            Q78=makeQuery(id+"F1.opExtrude","CAP_EDGE",EDGE,{"disambiguationData":[OSD([sQuery(id+"F0.wireOp",EDGE,"E6.0")])],"isStart":false});
            var Q79;
            {var subQ0=sQuery(id+"F0.wireOp",EDGE,"E2.filletArc");var subQ1=sQuery(id+"F0.wireOp",EDGE,"E1.left");Q79=makeQuery(id+"F3.boolean.opBoolean","SPLIT",EDGE,{"disambiguationData":[TD([makeQuery(id+"F1.opExtrude","SWEPT_FACE",FACE,{"disambiguationData":[OSD([subQ0])]})])],"derivedFrom":makeQuery(id+"F1.opExtrude","CAP_EDGE",EDGE,{"disambiguationData":[OSD([subQ1])],"isStart":false})});}
            var Q80;
            {var subQ0=sQuery(id+"F0.wireOp",EDGE,"E5.filletArc");var subQ1=sQuery(id+"F0.wireOp",EDGE,"E1.left");Q80=makeQuery(id+"F3.boolean.opBoolean","SPLIT",EDGE,{"disambiguationData":[TD([makeQuery(id+"F1.opExtrude","SWEPT_FACE",FACE,{"disambiguationData":[OSD([subQ0])]})])],"derivedFrom":makeQuery(id+"F1.opExtrude","CAP_EDGE",EDGE,{"disambiguationData":[OSD([subQ1])],"isStart":false})});}
            var Q81;
            {var subQ0=makeQuery(id+"F1.opExtrude","SWEPT_FACE",FACE,{"disambiguationData":[OSD([sQuery(id+"F0.wireOp",EDGE,"E1.top")])]});var subQ1=makeQuery(id+"F7.opExtrude","SWEPT_FACE",FACE,{"disambiguationData":[OSD([sQuery(id+"F6.wireOp",EDGE,"E9.bottom")])]});Q81=makeQuery(id+"F11.boolean.opBoolean","SPLIT",EDGE,{"disambiguationData":[TD([makeQuery(id+"F1.opExtrude","SWEPT_FACE",FACE,{"disambiguationData":[OSD([sQuery(id+"F0.wireOp",EDGE,"E5.filletArc")])]})])],"derivedFrom":makeQuery(id+"F7.boolean.opBoolean","INTERSECT",EDGE,{"derivedFrom":[subQ0,subQ1]})});}
            var Q82;
            {var subQ0=sQuery(id+"F0.wireOp",EDGE,"E3.filletArc");var subQ1=sQuery(id+"F0.wireOp",EDGE,"E1.right");Q82=makeQuery(id+"F3.boolean.opBoolean","SPLIT",EDGE,{"disambiguationData":[TD([makeQuery(id+"F1.opExtrude","SWEPT_FACE",FACE,{"disambiguationData":[OSD([subQ0])]})])],"derivedFrom":makeQuery(id+"F1.opExtrude","CAP_EDGE",EDGE,{"disambiguationData":[OSD([subQ1])],"isStart":false})});}
            var Q83;
            {var subQ0=sQuery(id+"F0.wireOp",EDGE,"E4.filletArc");var subQ1=sQuery(id+"F0.wireOp",EDGE,"E1.right");Q83=makeQuery(id+"F3.boolean.opBoolean","SPLIT",EDGE,{"disambiguationData":[TD([makeQuery(id+"F1.opExtrude","SWEPT_FACE",FACE,{"disambiguationData":[OSD([subQ0])]})])],"derivedFrom":makeQuery(id+"F1.opExtrude","CAP_EDGE",EDGE,{"disambiguationData":[OSD([subQ1])],"isStart":false})});}
            var Q84;
            {var subQ0=sQuery(id+"F0.wireOp",EDGE,"E6.5");var subQ1=sQuery(id+"F0.wireOp",EDGE,"E6.4");Q84=makeQuery(id+"F3.boolean.opBoolean","SPLIT",EDGE,{"disambiguationData":[TD([makeQuery(id+"F1.opExtrude","SWEPT_FACE",FACE,{"disambiguationData":[OSD([subQ1])]})])],"derivedFrom":makeQuery(id+"F1.opExtrude","CAP_EDGE",EDGE,{"disambiguationData":[OSD([subQ0])],"isStart":false})});}
            var Q85;
            {var subQ0=sQuery(id+"F0.wireOp",EDGE,"E6.6");var subQ1=sQuery(id+"F0.wireOp",EDGE,"E6.5");Q85=makeQuery(id+"F3.boolean.opBoolean","SPLIT",EDGE,{"disambiguationData":[TD([makeQuery(id+"F1.opExtrude","SWEPT_FACE",FACE,{"disambiguationData":[OSD([subQ0])]})])],"derivedFrom":makeQuery(id+"F1.opExtrude","CAP_EDGE",EDGE,{"disambiguationData":[OSD([subQ1])],"isStart":false})});}
            var Q86;
            Q86=makeQuery(id+"F3.boolean.opBoolean","INTERSECT",EDGE,{"disambiguationData":[OD(0.0)],"derivedFrom":[makeQuery(id+"F1.opExtrude","CAP_FACE",FACE,{"disambiguationData":[OSD([sQuery(id+"F0.wireOp",EDGE,"E1.bottom"),sQuery(id+"F0.wireOp",EDGE,"E1.top"),sQuery(id+"F0.wireOp",EDGE,"E1.left"),sQuery(id+"F0.wireOp",EDGE,"E1.right"),sQuery(id+"F0.wireOp",EDGE,"E2.filletArc"),sQuery(id+"F0.wireOp",EDGE,"E3.filletArc"),sQuery(id+"F0.wireOp",EDGE,"E4.filletArc"),sQuery(id+"F0.wireOp",EDGE,"E5.filletArc"),sQuery(id+"F0.wireOp",EDGE,"E6.0"),sQuery(id+"F0.wireOp",EDGE,"E6.1"),sQuery(id+"F0.wireOp",EDGE,"E6.2"),sQuery(id+"F0.wireOp",EDGE,"E6.3"),sQuery(id+"F0.wireOp",EDGE,"E6.4"),sQuery(id+"F0.wireOp",EDGE,"E6.5"),sQuery(id+"F0.wireOp",EDGE,"E6.6"),sQuery(id+"F0.wireOp",EDGE,"E6.7")])],"isStart":false}),makeQuery(id+"F3.opExtrude","SWEPT_FACE",FACE,{"disambiguationData":[OSD([sQuery(id+"F2.wireOp",EDGE,"E7")])]})]});
            var Q87;
            Q87=makeQuery(id+"F1.opExtrude","SWEPT_EDGE",EDGE,{"disambiguationData":[OSD([sQuery(id+"F0.wireOp",EDGE,"E1.top"),sQuery(id+"F0.wireOp",EDGE,"E4.filletArc")])]});
            var Q88;
            Q88=makeQuery(id+"F1.opExtrude","SWEPT_FACE",FACE,{"disambiguationData":[OSD([sQuery(id+"F0.wireOp",EDGE,"E5.filletArc")])]});
            var Q89;
            Q89=makeQuery(id+"F1.opExtrude","SWEPT_EDGE",EDGE,{"disambiguationData":[OSD([sQuery(id+"F0.wireOp",EDGE,"E6.3"),sQuery(id+"F0.wireOp",EDGE,"E6.7")])]});
            var Q90;
            Q90=makeQuery(id+"F1.opExtrude","SWEPT_EDGE",EDGE,{"disambiguationData":[OSD([sQuery(id+"F0.wireOp",EDGE,"E6.6"),sQuery(id+"F0.wireOp",EDGE,"E6.7")])]});
            var Q91;
            {var subQ0=makeQuery(id+"F1.opExtrude","SWEPT_FACE",FACE,{"disambiguationData":[OSD([sQuery(id+"F0.wireOp",EDGE,"E1.top")])]});var subQ1=makeQuery(id+"F7.opExtrude","SWEPT_FACE",FACE,{"disambiguationData":[OSD([sQuery(id+"F6.wireOp",EDGE,"E9.bottom")])]});Q91=makeQuery(id+"F11.boolean.opBoolean","SPLIT",EDGE,{"disambiguationData":[TD([makeQuery(id+"F1.opExtrude","SWEPT_FACE",FACE,{"disambiguationData":[OSD([sQuery(id+"F0.wireOp",EDGE,"E4.filletArc")])]})])],"derivedFrom":makeQuery(id+"F7.boolean.opBoolean","INTERSECT",EDGE,{"derivedFrom":[subQ0,subQ1]})});}
            var Q92;
            Q92=makeQuery(id+"F1.opExtrude","CAP_EDGE",EDGE,{"disambiguationData":[OSD([sQuery(id+"F0.wireOp",EDGE,"E6.3")])],"isStart":true});
            var Q93;
            Q93=makeQuery(id+"F7.boolean.opBoolean","INTERSECT",EDGE,{"derivedFrom":[makeQuery(id+"F1.opExtrude","SWEPT_FACE",FACE,{"disambiguationData":[OSD([sQuery(id+"F0.wireOp",EDGE,"E6.3")])]}),makeQuery(id+"F7.opExtrude","SWEPT_FACE",FACE,{"disambiguationData":[OSD([sQuery(id+"F6.wireOp",EDGE,"E9.bottom")])]})]});
            var Q94;
            Q94=makeQuery(id+"F7.boolean.opBoolean","INTERSECT",EDGE,{"derivedFrom":[makeQuery(id+"F1.opExtrude","SWEPT_FACE",FACE,{"disambiguationData":[OSD([sQuery(id+"F0.wireOp",EDGE,"E6.6")])]}),makeQuery(id+"F7.opExtrude","SWEPT_FACE",FACE,{"disambiguationData":[OSD([sQuery(id+"F6.wireOp",EDGE,"E9.bottom")])]})]});
            var Q95;
            Q95=makeQuery(id+"F7.boolean.opBoolean","INTERSECT",EDGE,{"derivedFrom":[makeQuery(id+"F1.opExtrude","SWEPT_FACE",FACE,{"disambiguationData":[OSD([sQuery(id+"F0.wireOp",EDGE,"E6.3")])]}),makeQuery(id+"F7.opExtrude","SWEPT_FACE",FACE,{"disambiguationData":[OSD([sQuery(id+"F6.wireOp",EDGE,"E9.left")])]})]});
            var Q96;
            Q96=makeQuery(id+"F7.boolean.opBoolean","INTERSECT",EDGE,{"derivedFrom":[makeQuery(id+"F1.opExtrude","SWEPT_FACE",FACE,{"disambiguationData":[OSD([sQuery(id+"F0.wireOp",EDGE,"E6.6")])]}),makeQuery(id+"F7.opExtrude","SWEPT_FACE",FACE,{"disambiguationData":[OSD([sQuery(id+"F6.wireOp",EDGE,"E9.right")])]})]});
            var Q97;
            Q97=makeQuery(id+"F1.opExtrude","SWEPT_EDGE",EDGE,{"disambiguationData":[OSD([sQuery(id+"F0.wireOp",EDGE,"E6.0"),sQuery(id+"F0.wireOp",EDGE,"E6.2")])]});
            var Q98;
            Q98=makeQuery(id+"F1.opExtrude","SWEPT_EDGE",EDGE,{"disambiguationData":[OSD([sQuery(id+"F0.wireOp",EDGE,"E6.2"),sQuery(id+"F0.wireOp",EDGE,"E6.4")])]});
            var Q99;
            Q99=makeQuery(id+"F1.opExtrude","CAP_EDGE",EDGE,{"disambiguationData":[OSD([sQuery(id+"F0.wireOp",EDGE,"E2.filletArc")])],"isStart":true});
            var Q100;
            Q100=makeQuery(id+"F1.opExtrude","CAP_EDGE",EDGE,{"disambiguationData":[OSD([sQuery(id+"F0.wireOp",EDGE,"E6.0")])],"isStart":true});
            var Q101;
            Q101=makeQuery(id+"F1.opExtrude","CAP_EDGE",EDGE,{"disambiguationData":[OSD([sQuery(id+"F0.wireOp",EDGE,"E6.4")])],"isStart":true});
            var Q102;
            Q102=makeQuery(id+"F9.boolean.opBoolean","INTERSECT",EDGE,{"derivedFrom":[makeQuery(id+"F1.opExtrude","SWEPT_FACE",FACE,{"disambiguationData":[OSD([sQuery(id+"F0.wireOp",EDGE,"E6.4")])]}),makeQuery(id+"F9.opExtrude","SWEPT_FACE",FACE,{"disambiguationData":[OSD([sQuery(id+"F8.wireOp",EDGE,"E10.left")])]})]});
            var Q103;
            Q103=makeQuery(id+"F9.boolean.opBoolean","INTERSECT",EDGE,{"derivedFrom":[makeQuery(id+"F1.opExtrude","SWEPT_FACE",FACE,{"disambiguationData":[OSD([sQuery(id+"F0.wireOp",EDGE,"E2.filletArc")])]}),makeQuery(id+"F9.opExtrude","SWEPT_FACE",FACE,{"disambiguationData":[OSD([sQuery(id+"F8.wireOp",EDGE,"E10.right")])]})]});
            var Q104;
            Q104=makeQuery(id+"F9.boolean.opBoolean","INTERSECT",EDGE,{"derivedFrom":[makeQuery(id+"F1.opExtrude","SWEPT_FACE",FACE,{"disambiguationData":[OSD([sQuery(id+"F0.wireOp",EDGE,"E6.0")])]}),makeQuery(id+"F9.opExtrude","SWEPT_FACE",FACE,{"disambiguationData":[OSD([sQuery(id+"F8.wireOp",EDGE,"E10.right")])]})]});
            var Q105;
            Q105=makeQuery(id+"F11.boolean.opBoolean","COPY",EDGE,{"derivedFrom":makeQuery(id+"F11.opExtrude","SWEPT_EDGE",EDGE,{"disambiguationData":[OSD([sQuery(id+"F0.wireOp",EDGE,"E6.7"),sQuery(id+"F10.wireOp",EDGE,"E11.top"),sQuery(id+"F10.wireOp",EDGE,"E11.right")])]})});
            var Q106;
            Q106=makeQuery(id+"F11.boolean.opBoolean","COPY",EDGE,{"derivedFrom":makeQuery(id+"F11.opExtrude","CAP_EDGE",EDGE,{"disambiguationData":[OSD([sQuery(id+"F10.wireOp",EDGE,"E11.left")])],"isStart":true})});
            var Q107;
            Q107=makeQuery(id+"F11.boolean.opBoolean","SPLIT",FACE,{"disambiguationData":[TD([makeQuery(id+"F1.opExtrude","SWEPT_FACE",FACE,{"disambiguationData":[OSD([sQuery(id+"F0.wireOp",EDGE,"E5.filletArc")])]})])],"derivedFrom":makeQuery(id+"F7.boolean.opBoolean","COPY",FACE,{"derivedFrom":makeQuery(id+"F7.opExtrude","SWEPT_FACE",FACE,{"disambiguationData":[OSD([sQuery(id+"F6.wireOp",EDGE,"E9.bottom")])]})})});
            var Q108;
            Q108=makeQuery(id+"F11.boolean.opBoolean","COPY",EDGE,{"derivedFrom":makeQuery(id+"F11.opExtrude","CAP_EDGE",EDGE,{"disambiguationData":[OSD([sQuery(id+"F10.wireOp",EDGE,"E11.right")])],"isStart":true})});
            var Q109;
            Q109=makeQuery(id+"F11.boolean.opBoolean","SPLIT",FACE,{"disambiguationData":[TD([makeQuery(id+"F1.opExtrude","SWEPT_FACE",FACE,{"disambiguationData":[OSD([sQuery(id+"F0.wireOp",EDGE,"E4.filletArc")])]})])],"derivedFrom":makeQuery(id+"F7.boolean.opBoolean","COPY",FACE,{"derivedFrom":makeQuery(id+"F7.opExtrude","SWEPT_FACE",FACE,{"disambiguationData":[OSD([sQuery(id+"F6.wireOp",EDGE,"E9.bottom")])]})})});
            var Q110;
            Q110=makeQuery(id+"F11.boolean.opBoolean","INTERSECT",EDGE,{"derivedFrom":[makeQuery(id+"F7.boolean.opBoolean","COPY",FACE,{"derivedFrom":makeQuery(id+"F7.opExtrude","SWEPT_FACE",FACE,{"disambiguationData":[OSD([sQuery(id+"F6.wireOp",EDGE,"E9.bottom")])]})}),makeQuery(id+"F11.opExtrude","SWEPT_FACE",FACE,{"disambiguationData":[OSD([sQuery(id+"F10.wireOp",EDGE,"E11.left")])]})]});
            var Q111;
            Q111=makeQuery(id+"F11.boolean.opBoolean","INTERSECT",EDGE,{"derivedFrom":[makeQuery(id+"F7.boolean.opBoolean","COPY",FACE,{"derivedFrom":makeQuery(id+"F7.opExtrude","SWEPT_FACE",FACE,{"disambiguationData":[OSD([sQuery(id+"F6.wireOp",EDGE,"E9.bottom")])]})}),makeQuery(id+"F11.opExtrude","SWEPT_FACE",FACE,{"disambiguationData":[OSD([sQuery(id+"F10.wireOp",EDGE,"E11.right")])]})]});
            var Q112;
            {var subQ0=sQuery(id+"F0.wireOp",EDGE,"E4.filletArc");var subQ1=sQuery(id+"F0.wireOp",EDGE,"E1.top");Q112=makeQuery(id+"F11.boolean.opBoolean","SPLIT",EDGE,{"disambiguationData":[TD([makeQuery(id+"F1.opExtrude","SWEPT_FACE",FACE,{"disambiguationData":[OSD([subQ0])]})])],"derivedFrom":makeQuery(id+"F1.opExtrude","CAP_EDGE",EDGE,{"disambiguationData":[OSD([subQ1])],"isStart":false})});}
            var Q113;
            {var subQ0=sQuery(id+"F0.wireOp",EDGE,"E6.7");var subQ1=sQuery(id+"F0.wireOp",EDGE,"E6.3");Q113=makeQuery(id+"F11.boolean.opBoolean","SPLIT",EDGE,{"disambiguationData":[TD([makeQuery(id+"F1.opExtrude","SWEPT_FACE",FACE,{"disambiguationData":[OSD([subQ1])]})])],"derivedFrom":makeQuery(id+"F1.opExtrude","CAP_EDGE",EDGE,{"disambiguationData":[OSD([subQ0])],"isStart":false})});}
            var Q114;
            {var subQ0=sQuery(id+"F6.wireOp",EDGE,"E9.bottom");Q114=makeQuery(id+"F11.boolean.opBoolean","SPLIT",EDGE,{"disambiguationData":[TD([makeQuery(id+"F1.opExtrude","SWEPT_FACE",FACE,{"disambiguationData":[OSD([sQuery(id+"F0.wireOp",EDGE,"E6.3")])]})])],"derivedFrom":makeQuery(id+"F7.boolean.opBoolean","COPY",EDGE,{"derivedFrom":makeQuery(id+"F7.opExtrude","CAP_EDGE",EDGE,{"disambiguationData":[OSD([subQ0])],"isStart":true})})});}
            var Q115;
            Q115=makeQuery(id+"F1.opExtrude","CAP_EDGE",EDGE,{"disambiguationData":[OSD([sQuery(id+"F0.wireOp",EDGE,"E3.filletArc")])],"isStart":false});
            var Q116;
            Q116=makeQuery(id+"F1.opExtrude","SWEPT_EDGE",EDGE,{"disambiguationData":[OSD([sQuery(id+"F0.wireOp",EDGE,"E1.top"),sQuery(id+"F0.wireOp",EDGE,"E5.filletArc")])]});
            var Q117;
            Q117=makeQuery(id+"F7.boolean.opBoolean","INTERSECT",EDGE,{"derivedFrom":[makeQuery(id+"F1.opExtrude","SWEPT_FACE",FACE,{"disambiguationData":[OSD([sQuery(id+"F0.wireOp",EDGE,"E5.filletArc")])]}),makeQuery(id+"F7.opExtrude","SWEPT_FACE",FACE,{"disambiguationData":[OSD([sQuery(id+"F6.wireOp",EDGE,"E9.bottom")])]})]});
            var Q118;
            Q118=makeQuery(id+"F9.boolean.opBoolean","INTERSECT",EDGE,{"derivedFrom":[makeQuery(id+"F1.opExtrude","SWEPT_FACE",FACE,{"disambiguationData":[OSD([sQuery(id+"F0.wireOp",EDGE,"E2.filletArc")])]}),makeQuery(id+"F9.opExtrude","SWEPT_FACE",FACE,{"disambiguationData":[OSD([sQuery(id+"F8.wireOp",EDGE,"E10.bottom")])]})]});
            var Q119;
            Q119=makeQuery(id+"F7.boolean.opBoolean","COPY",EDGE,{"derivedFrom":makeQuery(id+"F7.opExtrude","SWEPT_EDGE",EDGE,{"disambiguationData":[OSD([sQuery(id+"F6.wireOp",EDGE,"E9.bottom"),sQuery(id+"F6.wireOp",EDGE,"E9.right")])]})});
            var Q120;
            Q120=makeQuery(id+"F1.opExtrude","CAP_EDGE",EDGE,{"disambiguationData":[OSD([sQuery(id+"F0.wireOp",EDGE,"E4.filletArc")])],"isStart":false});
            var Q121;
            Q121=makeQuery(id+"F1.opExtrude","SWEPT_EDGE",EDGE,{"disambiguationData":[OSD([sQuery(id+"F0.wireOp",EDGE,"E1.right"),sQuery(id+"F0.wireOp",EDGE,"E3.filletArc")])]});
            var Q122;
            Q122=makeQuery(id+"F7.boolean.opBoolean","INTERSECT",EDGE,{"derivedFrom":[makeQuery(id+"F1.opExtrude","SWEPT_FACE",FACE,{"disambiguationData":[OSD([sQuery(id+"F0.wireOp",EDGE,"E4.filletArc")])]}),makeQuery(id+"F7.opExtrude","SWEPT_FACE",FACE,{"disambiguationData":[OSD([sQuery(id+"F6.wireOp",EDGE,"E9.bottom")])]})]});
            var Q123;
            Q123=makeQuery(id+"F1.opExtrude","SWEPT_EDGE",EDGE,{"disambiguationData":[OSD([sQuery(id+"F0.wireOp",EDGE,"E1.right"),sQuery(id+"F0.wireOp",EDGE,"E4.filletArc")])]});
            var Q124;
            Q124=makeQuery(id+"F1.opExtrude","SWEPT_EDGE",EDGE,{"disambiguationData":[OSD([sQuery(id+"F0.wireOp",EDGE,"E1.left"),sQuery(id+"F0.wireOp",EDGE,"E5.filletArc")])]});
            var Q125;
            Q125=makeQuery(id+"F1.opExtrude","CAP_EDGE",EDGE,{"disambiguationData":[OSD([sQuery(id+"F0.wireOp",EDGE,"E5.filletArc")])],"isStart":false});
            var Q126;
            {var subQ0=sQuery(id+"F0.wireOp",EDGE,"E6.1");var subQ1=sQuery(id+"F0.wireOp",EDGE,"E6.0");Q126=makeQuery(id+"F3.boolean.opBoolean","SPLIT",EDGE,{"disambiguationData":[TD([makeQuery(id+"F1.opExtrude","SWEPT_FACE",FACE,{"disambiguationData":[OSD([subQ1])]})])],"derivedFrom":makeQuery(id+"F1.opExtrude","CAP_EDGE",EDGE,{"disambiguationData":[OSD([subQ0])],"isStart":false})});}
            var Q127;
            {var subQ0=sQuery(id+"F0.wireOp",EDGE,"E6.3");var subQ1=sQuery(id+"F0.wireOp",EDGE,"E6.1");Q127=makeQuery(id+"F3.boolean.opBoolean","SPLIT",EDGE,{"disambiguationData":[TD([makeQuery(id+"F1.opExtrude","SWEPT_FACE",FACE,{"disambiguationData":[OSD([subQ0])]})])],"derivedFrom":makeQuery(id+"F1.opExtrude","CAP_EDGE",EDGE,{"disambiguationData":[OSD([subQ1])],"isStart":false})});}
            var Q128;
            Q128=makeQuery(id+"F1.opExtrude","CAP_EDGE",EDGE,{"disambiguationData":[OSD([sQuery(id+"F0.wireOp",EDGE,"E4.filletArc")])],"isStart":true});
            var Q129;
            Q129=makeQuery(id+"F1.opExtrude","CAP_EDGE",EDGE,{"disambiguationData":[OSD([sQuery(id+"F0.wireOp",EDGE,"E5.filletArc")])],"isStart":true});
            var Q130;
            Q130=makeQuery(id+"F7.boolean.opBoolean","INTERSECT",EDGE,{"derivedFrom":[makeQuery(id+"F1.opExtrude","SWEPT_FACE",FACE,{"disambiguationData":[OSD([sQuery(id+"F0.wireOp",EDGE,"E5.filletArc")])]}),makeQuery(id+"F7.opExtrude","SWEPT_FACE",FACE,{"disambiguationData":[OSD([sQuery(id+"F6.wireOp",EDGE,"E9.left")])]})]});
            var Q131;
            Q131=makeQuery(id+"F7.boolean.opBoolean","INTERSECT",EDGE,{"derivedFrom":[makeQuery(id+"F1.opExtrude","SWEPT_FACE",FACE,{"disambiguationData":[OSD([sQuery(id+"F0.wireOp",EDGE,"E4.filletArc")])]}),makeQuery(id+"F7.opExtrude","SWEPT_FACE",FACE,{"disambiguationData":[OSD([sQuery(id+"F6.wireOp",EDGE,"E9.right")])]})]});
            var Q132;
            Q132=makeQuery(id+"F1.opExtrude","SWEPT_EDGE",EDGE,{"disambiguationData":[OSD([sQuery(id+"F0.wireOp",EDGE,"E1.bottom"),sQuery(id+"F0.wireOp",EDGE,"E3.filletArc")])]});
            var Q133;
            Q133=makeQuery(id+"F9.boolean.opBoolean","INTERSECT",EDGE,{"derivedFrom":[makeQuery(id+"F1.opExtrude","SWEPT_FACE",FACE,{"disambiguationData":[OSD([sQuery(id+"F0.wireOp",EDGE,"E6.0")])]}),makeQuery(id+"F9.opExtrude","SWEPT_FACE",FACE,{"disambiguationData":[OSD([sQuery(id+"F8.wireOp",EDGE,"E10.bottom")])]})]});
            var Q134;
            Q134=makeQuery(id+"F9.boolean.opBoolean","INTERSECT",EDGE,{"derivedFrom":[makeQuery(id+"F1.opExtrude","SWEPT_FACE",FACE,{"disambiguationData":[OSD([sQuery(id+"F0.wireOp",EDGE,"E6.4")])]}),makeQuery(id+"F9.opExtrude","SWEPT_FACE",FACE,{"disambiguationData":[OSD([sQuery(id+"F8.wireOp",EDGE,"E10.bottom")])]})]});
            var Q135;
            Q135=makeQuery(id+"F9.boolean.opBoolean","INTERSECT",EDGE,{"derivedFrom":[makeQuery(id+"F1.opExtrude","SWEPT_FACE",FACE,{"disambiguationData":[OSD([sQuery(id+"F0.wireOp",EDGE,"E3.filletArc")])]}),makeQuery(id+"F9.opExtrude","SWEPT_FACE",FACE,{"disambiguationData":[OSD([sQuery(id+"F8.wireOp",EDGE,"E10.left")])]})]});
            var Q136;
            Q136=makeQuery(id+"F9.boolean.opBoolean","INTERSECT",EDGE,{"derivedFrom":[makeQuery(id+"F1.opExtrude","SWEPT_FACE",FACE,{"disambiguationData":[OSD([sQuery(id+"F0.wireOp",EDGE,"E3.filletArc")])]}),makeQuery(id+"F9.opExtrude","SWEPT_FACE",FACE,{"disambiguationData":[OSD([sQuery(id+"F8.wireOp",EDGE,"E10.bottom")])]})]});
            var Q137;
            Q137=makeQuery(id+"F1.opExtrude","CAP_EDGE",EDGE,{"disambiguationData":[OSD([sQuery(id+"F0.wireOp",EDGE,"E3.filletArc")])],"isStart":true});
            fillet(context, id + "F12", {"entities" : qUnion([Q0, Q1, Q2, Q3, Q4, Q5, Q6, Q7, Q8, Q9, Q10, Q11, Q12, Q13, Q14, Q15, Q16, Q17, Q18, Q19, Q20, Q21, Q22, Q23, Q24, Q25, Q26, Q27, Q28, Q29, Q30, Q31, Q32, Q33, Q34, Q35, Q36, Q37, Q38, Q39, Q40, Q41, Q42, Q43, Q44, Q45, Q46, Q47, Q48, Q49, Q50, Q51, Q52, Q53, Q54, Q55, Q56, Q57, Q58, Q59, Q60, Q61, Q62, Q63, Q64, Q65, Q66, Q67, Q68, Q69, Q70, Q71, Q72, Q73, Q74, Q75, Q76, Q77, Q78, Q79, Q80, Q81, Q82, Q83, Q84, Q85, Q86, Q87, Q88, Q89, Q90, Q91, Q92, Q93, Q94, Q95, Q96, Q97, Q98, Q99, Q100, Q101, Q102, Q103, Q104, Q105, Q106, Q107, Q108, Q109, Q110, Q111, Q112, Q113, Q114, Q115, Q116, Q117, Q118, Q119, Q120, Q121, Q122, Q123, Q124, Q125, Q126, Q127, Q128, Q129, Q130, Q131, Q132, Q133, Q134, Q135, Q136, Q137]), "radius" : .3 * mm, "tangentPropagation" : true, "allowEdgeOverflow" : false});
        }
    });
